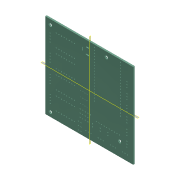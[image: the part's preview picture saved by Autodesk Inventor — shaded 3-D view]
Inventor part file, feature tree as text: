
AUTODESK INVENTOR PART (.ipt)
format: ipt  version: 2022 (Build 260153000, 153)  size: 378,368 bytes
history: native  units: mm
features: plane x2
ambient origin geometry x8: Origin, YZ Plane, XZ Plane, XY Plane, X Axis, Y Axis, Z Axis, Center Point
bodies: Volumenkörper1 (feature_tree)
feature tree (2):
  plane  "Arbeitsebene1"
  plane  "Arbeitsebene2"
